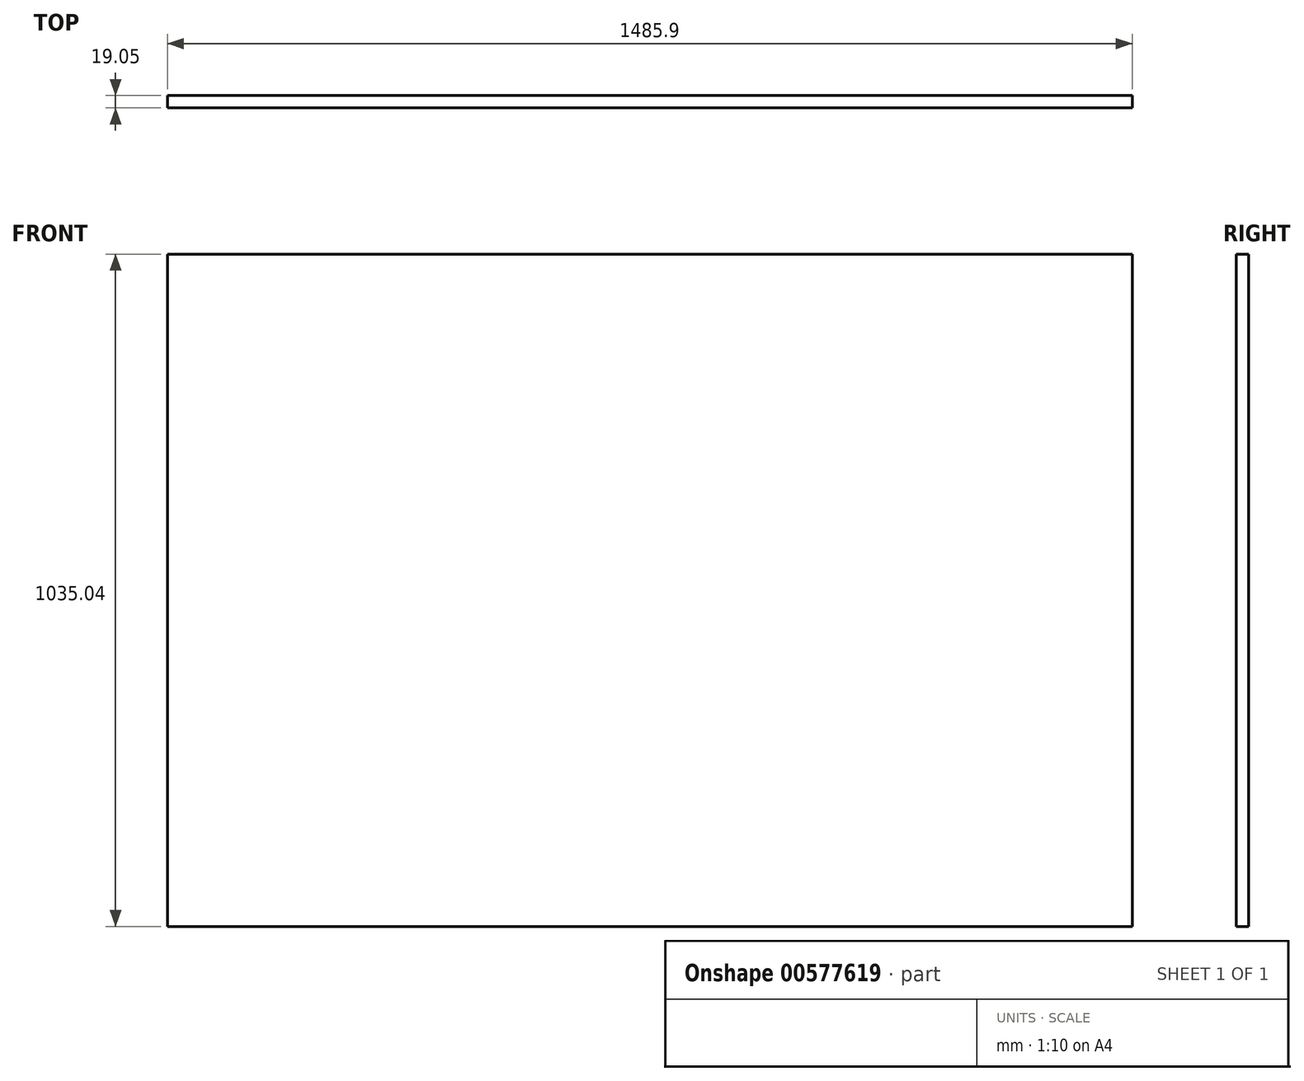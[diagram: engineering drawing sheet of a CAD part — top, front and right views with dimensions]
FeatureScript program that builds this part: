
annotation { "Feature Type Name" : "Feature", "Feature Type Description" : "" }
export const myFeature = defineFeature(function(context is Context, id is Id, definition is map)
    precondition{}
    {
        {
            var Q0;
            Q0=qCreatedBy(makeId("Front.planeOp"),FACE);
            var sketch = newSketch(context, id + "F0", { "sketchPlane" : qUnion([Q0])});
            skLineSegment(sketch, "E0.bottom", {"start": v(742.95, 517.53) * mm, "end": v(-742.95, 517.52) * mm});
            skLineSegment(sketch, "E0.top", {"start": v(742.95, -517.52) * mm, "end": v(-742.95, -517.53) * mm});
            skLineSegment(sketch, "E0.left", {"start": v(742.95, 517.53) * mm, "end": v(742.95, -517.52) * mm});
            skLineSegment(sketch, "E0.right", {"start": v(-742.95, 517.52) * mm, "end": v(-742.95, -517.53) * mm});
            skPoint(sketch, "E0.middle", {"position": v(0, 0) * mm});
            skSolve(sketch);
        }
        {
            var Q0;
            Q0=makeQuery(id+"F0.imprint","IMPRINT",FACE,{"disambiguationData":[TD([[makeQuery(id+"F0.imprint","IMPRINT",EDGE,{"derivedFrom":sQuery(id+"F0.wireOp",EDGE,"E0.bottom")}),1.0]])]});
            extrude(context, id + "F1", {"entities" : qUnion([Q0]), "depth" : 19.05 * mm, "offsetDistance" : 25.4 * mm});
        }
    });
